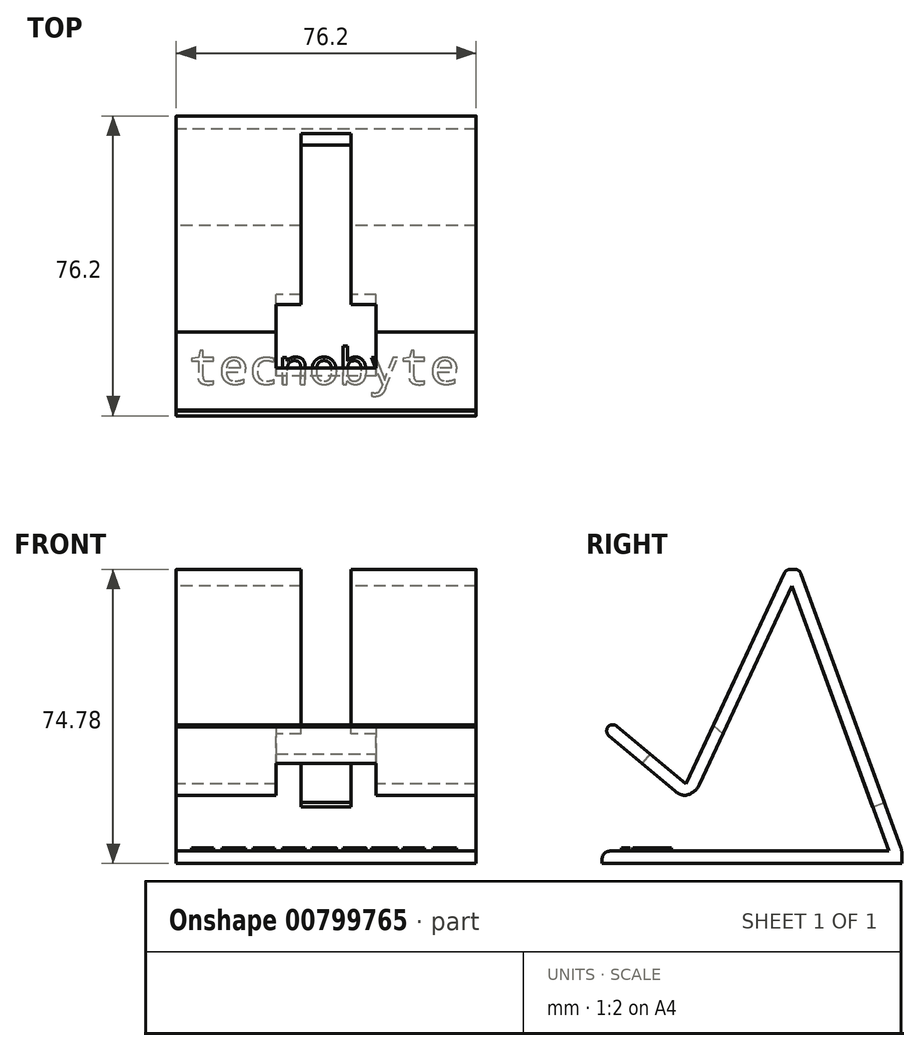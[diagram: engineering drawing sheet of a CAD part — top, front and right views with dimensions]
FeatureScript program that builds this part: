
annotation { "Feature Type Name" : "Feature", "Feature Type Description" : "" }
export const myFeature = defineFeature(function(context is Context, id is Id, definition is map)
    precondition{}
    {
        {
            var Q0;
            Q0=qCreatedBy(makeId("Top.planeOp"),FACE);
            var sketch = newSketch(context, id + "F0", { "sketchPlane" : qUnion([Q0])});
            skLineSegment(sketch, "E0.bottom", {"start": v(-50.93, 28.39) * mm, "end": v(25.27, 28.39) * mm});
            skLineSegment(sketch, "E0.top", {"start": v(-50.93, -47.81) * mm, "end": v(25.27, -47.81) * mm});
            skLineSegment(sketch, "E0.left", {"start": v(-50.93, 28.39) * mm, "end": v(-50.93, -47.81) * mm});
            skLineSegment(sketch, "E0.right", {"start": v(25.27, 28.39) * mm, "end": v(25.27, -47.81) * mm});
            skSolve(sketch);
        }
        {
            var Q0;
            Q0=qSketchRegion(id+"F0",true);
            extrude(context, id + "F1", {"entities" : qUnion([Q0]), "depth" : 3.17 * mm, "offsetDistance" : 25.4 * mm});
        }
        {
            var Q0;
            Q0=makeQuery(id+"F1.opExtrude","SWEPT_FACE",FACE,{"disambiguationData":[OSD([sQuery(id+"F0.wireOp",EDGE,"E0.left")])]});
            var sketch = newSketch(context, id + "F2", { "sketchPlane" : qUnion([Q0])});
            skLineSegment(sketch, "E1", {"start": v(-28.39, 3.17) * mm, "end": v(-2.33, 74.78) * mm});
            skLineSegment(sketch, "E2", {"start": v(-25, 3.18) * mm, "end": v(1.05, 74.78) * mm});
            skLineSegment(sketch, "E3", {"start": v(1.05, 74.78) * mm, "end": v(-2.33, 74.78) * mm});
            skLineSegment(sketch, "E4", {"start": v(27.89, 17.23) * mm, "end": v(1.05, 74.78) * mm});
            skLineSegment(sketch, "E5", {"start": v(47.35, 33.56) * mm, "end": v(27.89, 17.23) * mm});
            skLineSegment(sketch, "E6", {"start": v(-0.48, 70.56) * mm, "end": v(24.39, 17.23) * mm});
            skLineSegment(sketch, "E7", {"start": v(24.39, 17.23) * mm, "end": v(27.89, 17.23) * mm});
            skLineSegment(sketch, "E8", {"start": v(47.35, 33.56) * mm, "end": v(45.3, 35.99) * mm});
            skLineSegment(sketch, "E9", {"start": v(45.3, 35.99) * mm, "end": v(26.5, 20.2) * mm});
            skSolve(sketch);
        }
        {
            var Q0;
            Q0=qSketchRegion(id+"F2",true);
            var Q1;
            {var subQ6=sQuery(id+"F2.wireOp",EDGE,"E1");Q1=makeQuery(id+"F2.imprint","IMPRINT",FACE,{"disambiguationData":[TD([[makeQuery(id+"F2.imprint","IMPRINT",EDGE,{"derivedFrom":subQ6}),-1.0]])]});}
            extrude(context, id + "F3", {"entities" : qUnion([Q0, Q1]), "operationType" : NewBodyOperationType.ADD, "oppositeDirection" : true, "depth" : 76.2 * mm, "offsetDistance" : 25.4 * mm});
        }
        {
            var Q0;
            Q0=makeQuery(id+"F3.opExtrude","SWEPT_EDGE",EDGE,{"disambiguationData":[OSD([sQuery(id+"F2.wireOp",EDGE,"E2"),sQuery(id+"F2.wireOp",EDGE,"E3"),sQuery(id+"F2.wireOp",EDGE,"E4")])]});
            var Q1;
            Q1=makeQuery(id+"F3.opExtrude","SWEPT_EDGE",EDGE,{"disambiguationData":[OSD([sQuery(id+"F2.wireOp",EDGE,"E1"),sQuery(id+"F2.wireOp",EDGE,"E3")])]});
            fillet(context, id + "F4", {"entities" : qUnion([Q0, Q1]), "radius" : 1.71 * mm, "tangentPropagation" : true, "allowEdgeOverflow" : false});
        }
        {
            var Q0;
            {var subQ0=sQuery(id+"F0.wireOp",EDGE,"E0.bottom");Q0=makeQuery(id+"F3.boolean.opBoolean","MERGE",EDGE,{"derivedFrom":[makeQuery(id+"F1.opExtrude","CAP_EDGE",EDGE,{"disambiguationData":[OSD([subQ0])],"isStart":false}),makeQuery(id+"F3.opExtrude","SWEPT_EDGE",EDGE,{"disambiguationData":[OSD([subQ0,sQuery(id+"F0.wireOp",EDGE,"E0.left"),sQuery(id+"F2.wireOp",EDGE,"E1")])]})]});}
            fillet(context, id + "F5", {"entities" : qUnion([Q0]), "radius" : 5.08 * mm, "tangentPropagation" : true, "allowEdgeOverflow" : false});
        }
        {
            var Q0;
            Q0=makeQuery(id+"F3.opExtrude","SWEPT_EDGE",EDGE,{"disambiguationData":[OSD([sQuery(id+"F2.wireOp",EDGE,"E8"),sQuery(id+"F2.wireOp",EDGE,"E9")])]});
            var Q1;
            Q1=makeQuery(id+"F3.opExtrude","SWEPT_EDGE",EDGE,{"disambiguationData":[OSD([sQuery(id+"F2.wireOp",EDGE,"E5"),sQuery(id+"F2.wireOp",EDGE,"E8")])]});
            fillet(context, id + "F6", {"entities" : qUnion([Q0, Q1]), "radius" : 1.71 * mm, "tangentPropagation" : true, "allowEdgeOverflow" : false});
        }
        {
            var Q0;
            Q0=makeQuery(id+"F3.opExtrude","SWEPT_EDGE",EDGE,{"disambiguationData":[OSD([sQuery(id+"F2.wireOp",EDGE,"E6"),sQuery(id+"F2.wireOp",EDGE,"E7")])]});
            var Q1;
            Q1=makeQuery(id+"F3.opExtrude","SWEPT_EDGE",EDGE,{"disambiguationData":[OSD([sQuery(id+"F2.wireOp",EDGE,"E4"),sQuery(id+"F2.wireOp",EDGE,"E5"),sQuery(id+"F2.wireOp",EDGE,"E7")])]});
            fillet(context, id + "F7", {"entities" : qUnion([Q0, Q1]), "radius" : 5.08 * mm, "tangentPropagation" : true, "allowEdgeOverflow" : false});
        }
        {
            var Q0;
            Q0=makeQuery(id+"F1.opExtrude","CAP_EDGE",EDGE,{"disambiguationData":[OSD([sQuery(id+"F0.wireOp",EDGE,"E0.top")])],"isStart":false});
            fillet(context, id + "F8", {"entities" : qUnion([Q0]), "radius" : 2 * mm, "tangentPropagation" : true, "allowEdgeOverflow" : false});
        }
        {
            var Q0;
            Q0=makeQuery(id+"F3.opExtrude","SWEPT_FACE",FACE,{"disambiguationData":[OSD([sQuery(id+"F2.wireOp",EDGE,"E1")])]});
            var sketch = newSketch(context, id + "F9", { "sketchPlane" : qUnion([Q0])});
            skLineSegment(sketch, "E10.bottom", {"start": v(6.48, 6.38) * mm, "end": v(19.18, 6.38) * mm});
            skLineSegment(sketch, "E10.top", {"start": v(6.48, 82.58) * mm, "end": v(19.18, 82.58) * mm});
            skLineSegment(sketch, "E10.left", {"start": v(6.48, 6.38) * mm, "end": v(6.48, 82.58) * mm});
            skLineSegment(sketch, "E10.right", {"start": v(19.18, 6.38) * mm, "end": v(19.18, 82.58) * mm});
            skSolve(sketch);
        }
        {
            var Q0;
            Q0=qSketchRegion(id+"F9",true);
            var Q1;
            Q1=makeQuery(id+"F3.opExtrude","SWEPT_FACE",FACE,{"disambiguationData":[OSD([sQuery(id+"F2.wireOp",EDGE,"E9")])]});
            extrude(context, id + "F10", {"entities" : qUnion([Q0]), "operationType" : NewBodyOperationType.REMOVE, "endBound" : BoundingType.UP_TO_SURFACE, "oppositeDirection" : true, "depth" : 38.1 * mm, "endBoundEntityFace" : qUnion([Q1]), "offsetDistance" : 25.4 * mm});
        }
        {
            var Q0;
            Q0=makeQuery(id+"F3.opExtrude","SWEPT_FACE",FACE,{"disambiguationData":[OSD([sQuery(id+"F2.wireOp",EDGE,"E5")])]});
            var sketch = newSketch(context, id + "F11", { "sketchPlane" : qUnion([Q0])});
            skLineSegment(sketch, "E11.bottom", {"start": v(-0.13, 45.2) * mm, "end": v(-25.53, 45.2) * mm});
            skLineSegment(sketch, "E11.top", {"start": v(-0.13, 25.32) * mm, "end": v(-25.53, 25.32) * mm});
            skLineSegment(sketch, "E11.left", {"start": v(-0.13, 45.2) * mm, "end": v(-0.13, 25.32) * mm});
            skLineSegment(sketch, "E11.right", {"start": v(-25.53, 45.2) * mm, "end": v(-25.53, 25.32) * mm});
            skSolve(sketch);
        }
        {
            var Q0;
            Q0=qSketchRegion(id+"F11",true);
            extrude(context, id + "F12", {"entities" : qUnion([Q0]), "operationType" : NewBodyOperationType.REMOVE, "oppositeDirection" : true, "depth" : 19.05 * mm, "offsetDistance" : 25.4 * mm});
        }
        {
            var Q0;
            Q0=makeQuery(id+"F0.imprint","IMPRINT",FACE,{"disambiguationData":[TD([[makeQuery(id+"F0.imprint","IMPRINT",EDGE,{"derivedFrom":sQuery(id+"F0.wireOp",EDGE,"E0.bottom")}),-1.0]])]});
            var sketch = newSketch(context, id + "F13", { "sketchPlane" : qUnion([Q0])});
            skText(sketch, "E12", { "text": "tecnobyte", "fontName": "DroidSansMono.ttf"});
            const initialGuessF13  = {"E12": [-0.04783, -0.03984, 1, 0, 0.00919]};
            skSetInitialGuess(sketch, initialGuessF13);
            skSolve(sketch);
        }
        {
            var Q0;
            Q0 = qSketchRegion(id + "F13", true);
            extrude(context, id + "F14", {"entities" : qUnion([Q0]), "operationType" : NewBodyOperationType.ADD, "depth" : 4 * mm, "offsetDistance" : 25 * mm});
        }
    });
